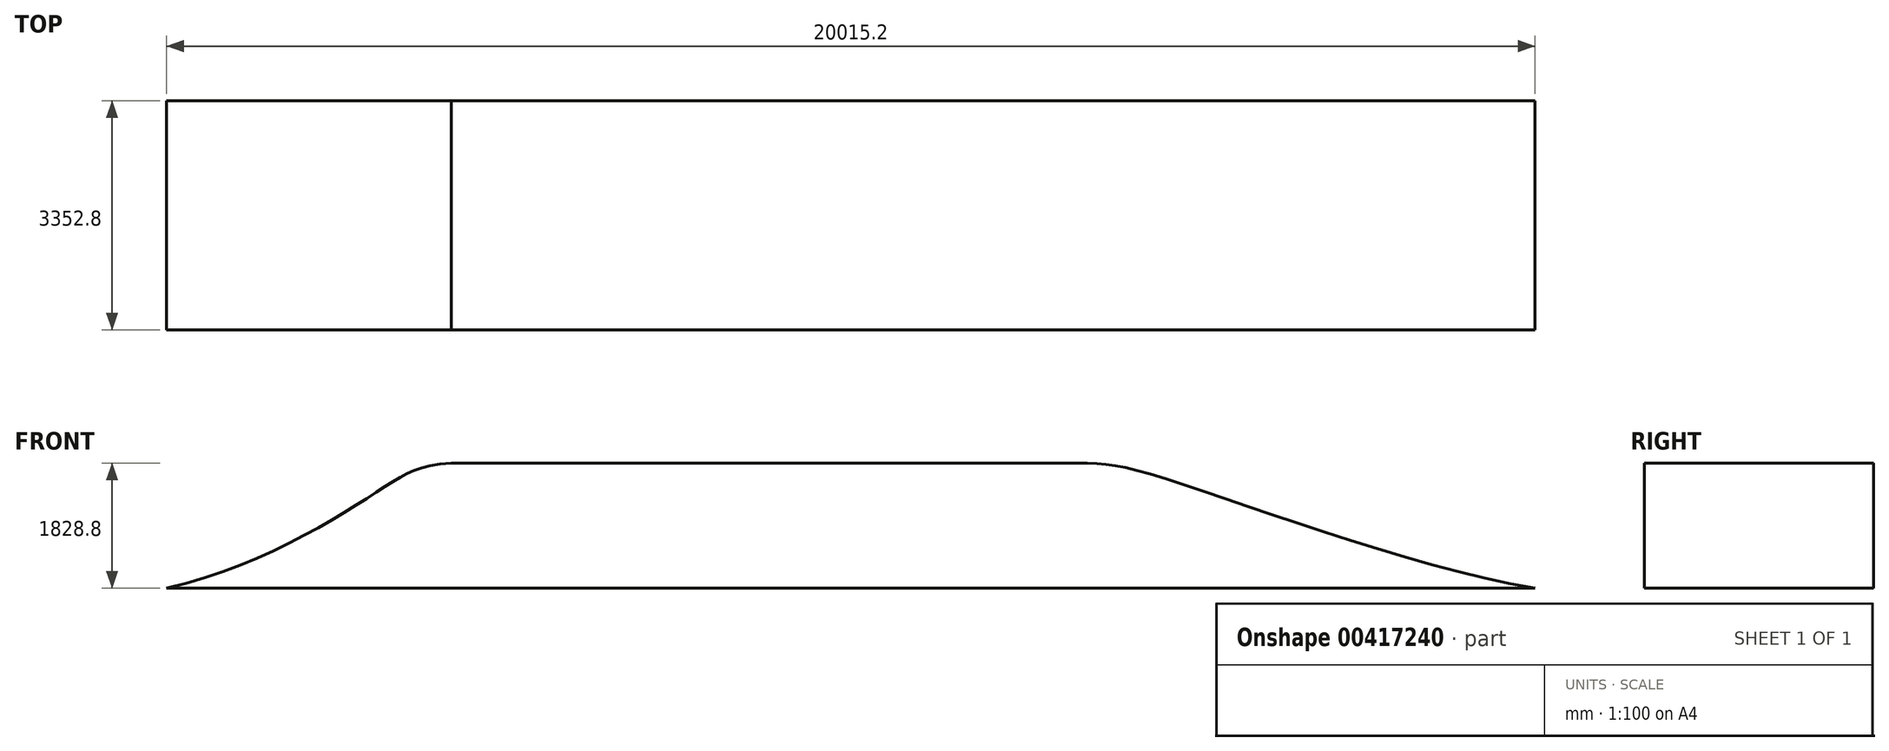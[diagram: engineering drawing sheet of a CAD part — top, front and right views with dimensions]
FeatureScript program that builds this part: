
annotation { "Feature Type Name" : "Feature", "Feature Type Description" : "" }
export const myFeature = defineFeature(function(context is Context, id is Id, definition is map)
    precondition{}
    {
        {
            var Q0;
            Q0=qCreatedBy(makeId("Front.planeOp"),FACE);
            var sketch = newSketch(context, id + "F0", { "sketchPlane" : qUnion([Q0])});
            skLineSegment(sketch, "E0", {"start": v(0, 0) * mm, "end": v(20015.2, 0) * mm});
            skLineSegment(sketch, "E1", {"start": v(4165.6, 1828.8) * mm, "end": v(13309.6, 1828.8) * mm});
            skLineSegment(sketch, "E2", {"start": v(13309.6, 1828.8) * mm, "end": v(13309.6, 0) * mm, "construction": true});
            skLineSegment(sketch, "E3", {"start": v(4165.6, 1828.8) * mm, "end": v(4165.6, 0) * mm, "construction": true});
            skFitSpline(sketch, "E4", {"points": [v(0, 0) * mm, v(3175.72, 1474.2) * mm, v(4165.6, 1828.8) * mm], "startDerivative": vector(6540.1, 1470.55) * mm, "endDerivative": vector(4179.61, 275.7) * mm});
            skFitSpline(sketch, "E5", {"points": [v(13309.6, 1828.8) * mm, v(14351, 1680.35) * mm, v(20015.2, 0) * mm], "startDerivative": vector(3747.3, -31.04) * mm, "endDerivative": vector(8126.32, -1351.68) * mm});
            skSolve(sketch);
        }
        {
            var Q0;
            Q0=makeQuery(id+"F0.imprint","IMPRINT",FACE,{"disambiguationData":[TD([[makeQuery(id+"F0.imprint","IMPRINT",EDGE,{"derivedFrom":sQuery(id+"F0.wireOp",EDGE,"E0")}),1.0]])]});
            extrude(context, id + "F1", {"entities" : qUnion([Q0]), "depth" : 3352.8 * mm});
        }
    });
